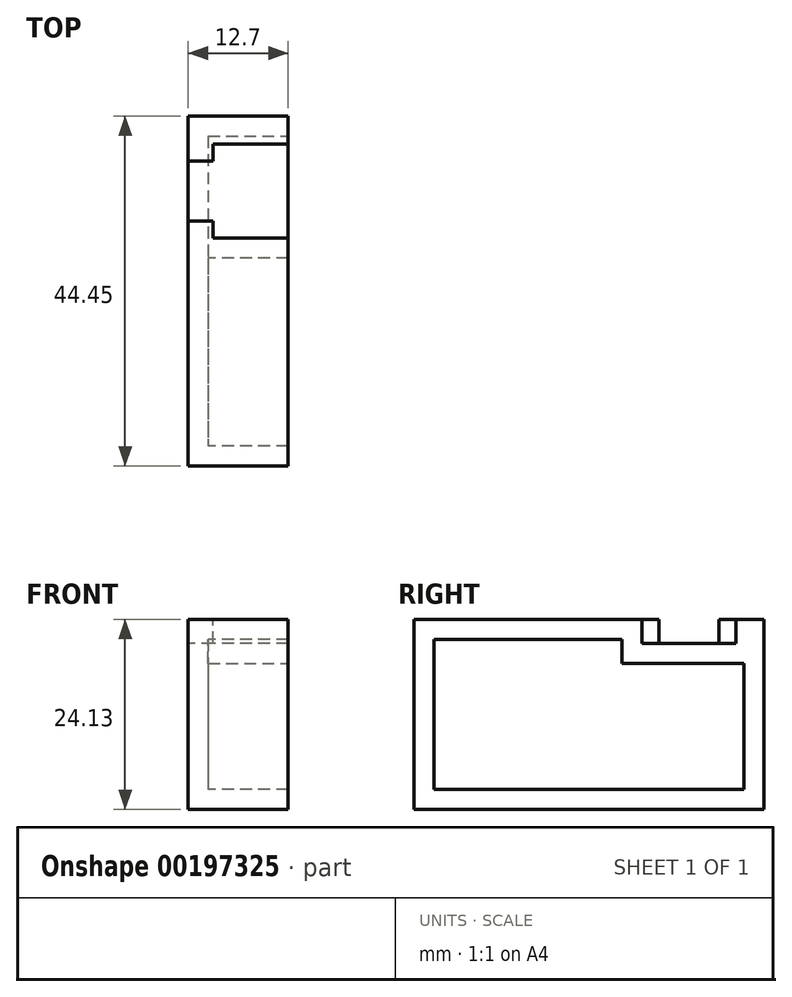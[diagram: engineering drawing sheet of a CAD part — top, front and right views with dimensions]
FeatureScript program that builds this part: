
annotation { "Feature Type Name" : "Feature", "Feature Type Description" : "" }
export const myFeature = defineFeature(function(context is Context, id is Id, definition is map)
    precondition{}
    {
        {
            var Q0;
            Q0=qCreatedBy(makeId("Top.planeOp"),FACE);
            var sketch = newSketch(context, id + "F0", { "sketchPlane" : qUnion([Q0])});
            skLineSegment(sketch, "E0.bottom", {"start": v(6.35, 9.53) * mm, "end": v(-6.35, 9.53) * mm});
            skLineSegment(sketch, "E0.top", {"start": v(6.35, -9.52) * mm, "end": v(-6.35, -9.52) * mm});
            skLineSegment(sketch, "E0.left", {"start": v(6.35, 9.53) * mm, "end": v(6.35, -9.52) * mm});
            skLineSegment(sketch, "E0.right", {"start": v(-6.35, 9.53) * mm, "end": v(-6.35, -9.52) * mm});
            skPoint(sketch, "E0.middle", {"position": v(0, 0) * mm});
            skSolve(sketch);
        }
        {
            var Q0;
            Q0 = qSketchRegion(id + "F0", true);
            extrude(context, id + "F1", {"entities" : qUnion([Q0]), "depth" : 5.08 * mm});
        }
        {
            var Q0;
            Q0=makeQuery(id+"F1.opExtrude","CAP_FACE",FACE,{"disambiguationData":[OSD([sQuery(id+"F0.wireOp",EDGE,"E0.bottom"),sQuery(id+"F0.wireOp",EDGE,"E0.top"),sQuery(id+"F0.wireOp",EDGE,"E0.left"),sQuery(id+"F0.wireOp",EDGE,"E0.right")])],"isStart":false});
            var sketch = newSketch(context, id + "F2", { "sketchPlane" : qUnion([Q0])});
            skLineSegment(sketch, "E1.bottom", {"start": v(9.15, 5.97) * mm, "end": v(-3.17, 5.97) * mm});
            skLineSegment(sketch, "E1.top", {"start": v(9.15, -5.97) * mm, "end": v(-3.18, -5.97) * mm});
            skLineSegment(sketch, "E1.left", {"start": v(9.15, 5.97) * mm, "end": v(9.15, -5.97) * mm});
            skLineSegment(sketch, "E1.right", {"start": v(-3.17, 5.97) * mm, "end": v(-3.18, -5.97) * mm});
            skPoint(sketch, "E1.middle", {"position": v(2.99, 0) * mm});
            skSolve(sketch);
        }
        {
            var Q0;
            Q0 = qSketchRegion(id + "F2", true);
            extrude(context, id + "F3", {"entities" : qUnion([Q0]), "operationType" : NewBodyOperationType.REMOVE, "oppositeDirection" : true, "depth" : 3.05 * mm});
        }
        {
            var Q0;
            Q0=makeQuery(id+"F1.opExtrude","CAP_FACE",FACE,{"disambiguationData":[OSD([sQuery(id+"F0.wireOp",EDGE,"E0.bottom"),sQuery(id+"F0.wireOp",EDGE,"E0.top"),sQuery(id+"F0.wireOp",EDGE,"E0.left"),sQuery(id+"F0.wireOp",EDGE,"E0.right")])],"isStart":false});
            var sketch = newSketch(context, id + "F4", { "sketchPlane" : qUnion([Q0])});
            skLineSegment(sketch, "E2.bottom", {"start": v(-6.78, 3.81) * mm, "end": v(-3.18, 3.81) * mm});
            skLineSegment(sketch, "E2.top", {"start": v(-6.78, -3.8) * mm, "end": v(-3.18, -3.8) * mm});
            skLineSegment(sketch, "E2.left", {"start": v(-6.78, 3.81) * mm, "end": v(-6.78, -3.8) * mm});
            skLineSegment(sketch, "E2.right", {"start": v(-3.17, 3.81) * mm, "end": v(-3.17, -3.8) * mm});
            skPoint(sketch, "E2.middle", {"position": v(-4.98, 0) * mm});
            skPoint(sketch, "E2.middle.positionSnap0", {"position": v(-3.17, 0) * mm});
            skPoint(sketch, "E2.centerSnap0", {"position": v(-3.17, 0) * mm});
            skSolve(sketch);
        }
        {
            var Q0;
            Q0 = qSketchRegion(id + "F4", true);
            var Q1;
            Q1=makeQuery(id+"F3.boolean.opBoolean","COPY",FACE,{"derivedFrom":makeQuery(id+"F3.opExtrude","CAP_FACE",FACE,{"disambiguationData":[OSD([sQuery(id+"F2.wireOp",EDGE,"E1.bottom"),sQuery(id+"F2.wireOp",EDGE,"E1.top"),sQuery(id+"F2.wireOp",EDGE,"E1.left"),sQuery(id+"F2.wireOp",EDGE,"E1.right")])],"isStart":false})});
            extrude(context, id + "F5", {"entities" : qUnion([Q0]), "operationType" : NewBodyOperationType.REMOVE, "endBound" : BoundingType.UP_TO_SURFACE, "oppositeDirection" : true, "endBoundEntityFace" : qUnion([Q1]), "depth" : 2.13 * mm});
        }
        {
            var Q0;
            Q0=makeQuery(id+"F1.opExtrude","SWEPT_FACE",FACE,{"disambiguationData":[OSD([sQuery(id+"F0.wireOp",EDGE,"E0.top")])]});
            extrude(context, id + "F6", {"entities" : qUnion([Q0]), "operationType" : NewBodyOperationType.ADD, "depth" : 25.4 * mm});
        }
        {
            var Q0;
            {var subQ0=sQuery(id+"F0.wireOp",EDGE,"E0.top");Q0=makeQuery(id+"F6.boolean.opBoolean","MERGE",FACE,{"derivedFrom":[makeQuery(id+"F1.opExtrude","CAP_FACE",FACE,{"disambiguationData":[OSD([sQuery(id+"F0.wireOp",EDGE,"E0.bottom"),subQ0,sQuery(id+"F0.wireOp",EDGE,"E0.left"),sQuery(id+"F0.wireOp",EDGE,"E0.right")])],"isStart":true}),makeQuery(id+"F6.opExtrude","SWEPT_FACE",FACE,{"disambiguationData":[OSD([subQ0]),TDD([makeQuery(id+"F1.opExtrude","CAP_EDGE",EDGE,{"disambiguationData":[OSD([subQ0])],"isStart":true})])]})]});}
            extrude(context, id + "F7", {"entities" : qUnion([Q0]), "operationType" : NewBodyOperationType.ADD, "depth" : 19.05 * mm});
        }
        {
            var Q0;
            {var subQ0=sQuery(id+"F0.wireOp",EDGE,"E0.left");var subQ1=sQuery(id+"F0.wireOp",EDGE,"E0.top");Q0=makeQuery(id+"F7.boolean.opBoolean","MERGE",FACE,{"derivedFrom":[makeQuery(id+"F6.boolean.opBoolean","MERGE",FACE,{"derivedFrom":[makeQuery(id+"F1.opExtrude","SWEPT_FACE",FACE,{"disambiguationData":[OSD([subQ0])]}),makeQuery(id+"F6.opExtrude","SWEPT_FACE",FACE,{"disambiguationData":[OSD([subQ1,subQ0])]})]}),makeQuery(id+"F7.opExtrude","SWEPT_FACE",FACE,{"disambiguationData":[OSD([subQ1,subQ0])]})]});}
            shell(context, id + "F8", {"entities" : qUnion([Q0]), "thickness" : 2.54 * mm});
        }
    });
